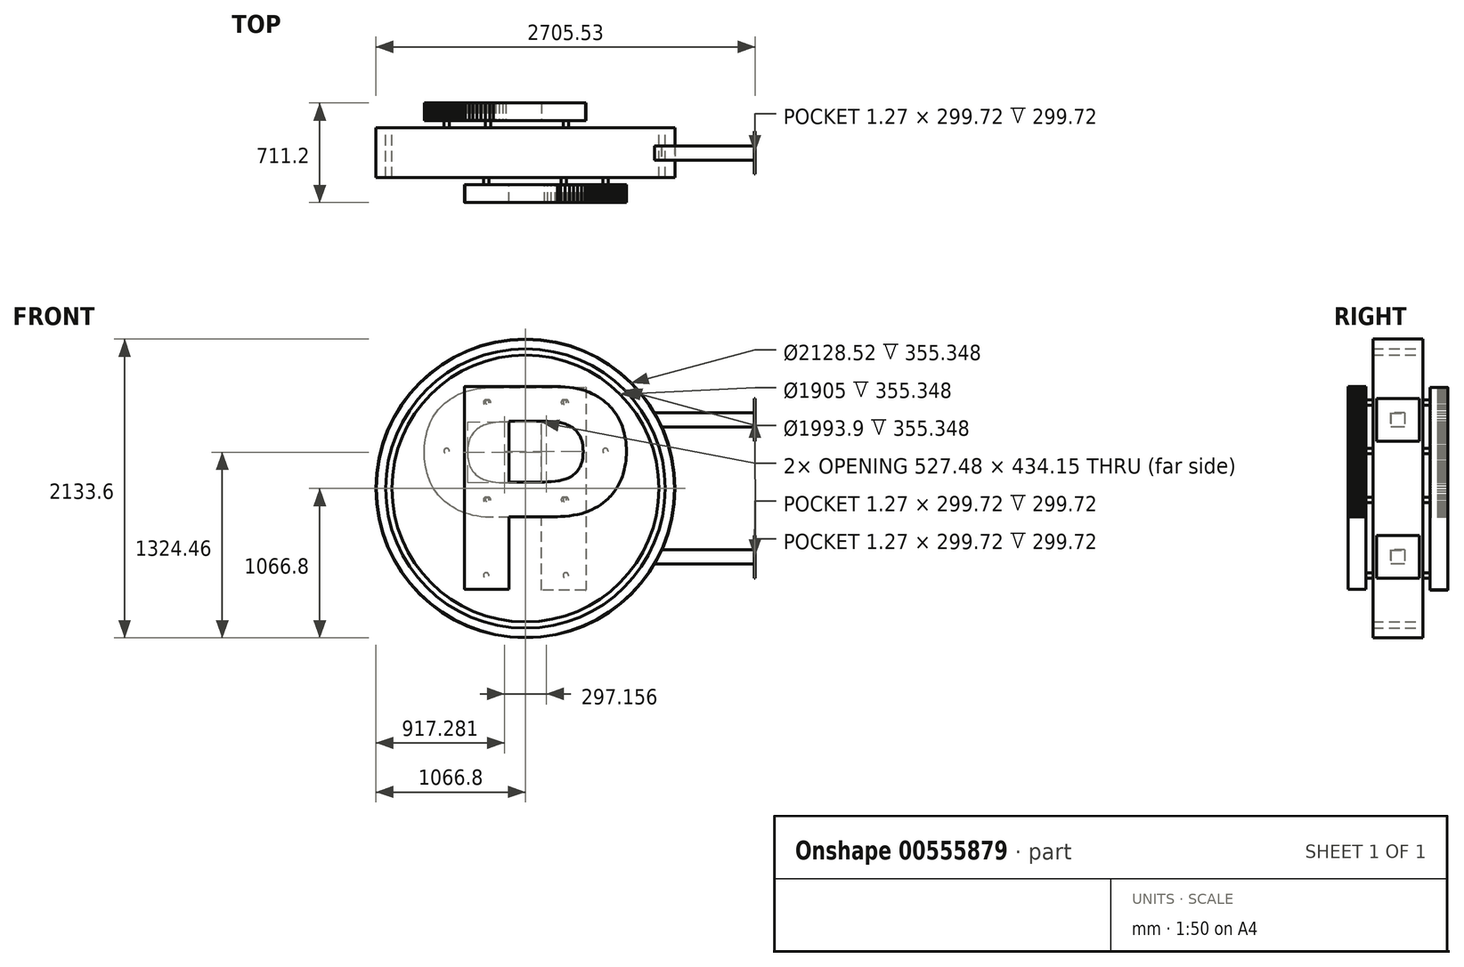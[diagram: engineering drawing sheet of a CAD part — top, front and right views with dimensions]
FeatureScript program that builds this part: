
annotation { "Feature Type Name" : "Feature", "Feature Type Description" : "" }
export const myFeature = defineFeature(function(context is Context, id is Id, definition is map)
    precondition{}
    {
        {
            var Q0;
            Q0=qCreatedBy(makeId("Front.planeOp"),FACE);
            var sketch = newSketch(context, id + "F0", { "sketchPlane" : qUnion([Q0])});
            skCircle(sketch, "E0", {"center": v(-32.18, 27.44) * mm, "radius": 1066.8 * mm});
            skSolve(sketch);
        }
        {
            var Q0;
            Q0 = qSketchRegion(id + "F0", true);
            extrude(context, id + "F1", {"entities" : qUnion([Q0]), "oppositeDirection" : true, "depth" : 355.6 * mm, "offsetDistance" : 25.4 * mm});
        }
        {
            var Q0;
            Q0=qCreatedBy(makeId("Right.planeOp"),FACE);
            var sketch = newSketch(context, id + "F2", { "sketchPlane" : qUnion([Q0])});
            skLineSegment(sketch, "E1.bottom", {"start": v(-1.34, 1094.24) * mm, "end": v(356.95, 1094.24) * mm});
            skLineSegment(sketch, "E1.top", {"start": v(-1.34, -1039.36) * mm, "end": v(356.95, -1039.36) * mm});
            skLineSegment(sketch, "E1.left", {"start": v(-1.34, 1094.24) * mm, "end": v(-1.34, -1039.36) * mm});
            skLineSegment(sketch, "E2", {"start": v(-1.34, 27.44) * mm, "end": v(356.95, 27.44) * mm});
            skLineSegment(sketch, "E3.bottom", {"start": v(125.66, 567.19) * mm, "end": v(227.26, 567.19) * mm});
            skLineSegment(sketch, "E3.top", {"start": v(125.66, 465.59) * mm, "end": v(227.26, 465.59) * mm});
            skLineSegment(sketch, "E3.left", {"start": v(125.66, 567.19) * mm, "end": v(125.66, 465.59) * mm});
            skLineSegment(sketch, "E3.right", {"start": v(227.26, 567.19) * mm, "end": v(227.26, 465.59) * mm});
            skLineSegment(sketch, "E4.bottom", {"start": v(125.66, -410.71) * mm, "end": v(227.26, -410.71) * mm});
            skLineSegment(sketch, "E4.top", {"start": v(125.66, -512.31) * mm, "end": v(227.26, -512.31) * mm});
            skLineSegment(sketch, "E4.left", {"start": v(125.66, -410.71) * mm, "end": v(125.66, -512.31) * mm});
            skLineSegment(sketch, "E4.right", {"start": v(227.26, -410.71) * mm, "end": v(227.26, -512.31) * mm});
            skSolve(sketch);
        }
        {
            var Q0;
            Q0 = qSketchRegion(id + "F2", true);
            extrude(context, id + "F3", {"entities" : qUnion([Q0]), "operationType" : NewBodyOperationType.ADD, "depth" : 1600.2 * mm, "offsetDistance" : 25.4 * mm});
        }
        {
            var Q0;
            Q0=makeQuery(id+"F3.opExtrude","CAP_FACE",FACE,{"disambiguationData":[OSD([sQuery(id+"F2.wireOp",EDGE,"E3.bottom"),sQuery(id+"F2.wireOp",EDGE,"E3.top"),sQuery(id+"F2.wireOp",EDGE,"E3.left"),sQuery(id+"F2.wireOp",EDGE,"E3.right")])],"isStart":false});
            var sketch = newSketch(context, id + "F4", { "sketchPlane" : qUnion([Q0])});
            skLineSegment(sketch, "E5.bottom", {"start": v(25.4, 668.79) * mm, "end": v(330.2, 668.79) * mm});
            skLineSegment(sketch, "E5.top", {"start": v(25.4, 363.99) * mm, "end": v(330.2, 363.99) * mm});
            skLineSegment(sketch, "E5.left", {"start": v(25.4, 668.79) * mm, "end": v(25.4, 363.99) * mm});
            skLineSegment(sketch, "E5.right", {"start": v(330.2, 668.79) * mm, "end": v(330.2, 363.99) * mm});
            skLineSegment(sketch, "E6.bottom", {"start": v(25.4, -309.11) * mm, "end": v(330.2, -309.11) * mm});
            skLineSegment(sketch, "E6.top", {"start": v(25.4, -613.91) * mm, "end": v(330.2, -613.91) * mm});
            skLineSegment(sketch, "E6.left", {"start": v(25.4, -309.11) * mm, "end": v(25.4, -613.91) * mm});
            skLineSegment(sketch, "E6.right", {"start": v(330.2, -309.11) * mm, "end": v(330.2, -613.91) * mm});
            skSolve(sketch);
        }
        {
            var Q0;
            Q0 = qSketchRegion(id + "F4", true);
            extrude(context, id + "F5", {"entities" : qUnion([Q0]), "operationType" : NewBodyOperationType.ADD, "depth" : 6.35 * mm, "offsetDistance" : 25.4 * mm});
        }
        {
            var Q0;
            Q0=makeQuery(id+"F1.opExtrude","CAP_FACE",FACE,{"disambiguationData":[OSD([sQuery(id+"F0.wireOp",EDGE,"E0")])],"isStart":false});
            var sketch = newSketch(context, id + "F6", { "sketchPlane" : qUnion([Q0])});
            skCircle(sketch, "E7", {"center": v(32.18, 27.44) * mm, "radius": 952.5 * mm});
            skCircle(sketch, "E8", {"center": v(32.18, 27.44) * mm, "radius": 996.95 * mm});
            skCircle(sketch, "E9", {"center": v(32.18, 27.44) * mm, "radius": 1066.8 * mm});
            skSolve(sketch);
        }
        {
            var Q0;
            Q0=makeQuery(id+"F1.opExtrude","CAP_FACE",FACE,{"disambiguationData":[OSD([sQuery(id+"F0.wireOp",EDGE,"E0")])],"isStart":false});
            var Q1;
            Q1=makeQuery(id+"F1.opExtrude","CAP_FACE",FACE,{"disambiguationData":[OSD([sQuery(id+"F0.wireOp",EDGE,"E0")])],"isStart":true});
            shell(context, id + "F7", {"entities" : qUnion([Q0, Q1]), "thickness" : 2.54 * mm});
        }
        {
            var Q0;
            Q0=makeQuery(id+"F6.imprint","IMPRINT",FACE,{"disambiguationData":[TD([[makeQuery(id+"F6.imprint","IMPRINT",EDGE,{"derivedFrom":sQuery(id+"F6.wireOp",EDGE,"E8")}),-1.0]])]});
            extrude(context, id + "F8", {"entities" : qUnion([Q0]), "oppositeDirection" : true, "depth" : 355.6 * mm, "offsetDistance" : 25.4 * mm});
        }
        {
            var Q0;
            Q0=makeQuery(id+"F6.imprint","IMPRINT",FACE,{"disambiguationData":[TD([[makeQuery(id+"F6.imprint","IMPRINT",EDGE,{"derivedFrom":sQuery(id+"F6.wireOp",EDGE,"E7")}),-1.0]])]});
            extrude(context, id + "F9", {"entities" : qUnion([Q0]), "oppositeDirection" : true, "depth" : 355.6 * mm, "offsetDistance" : 25.4 * mm});
        }
        {
            var Q0;
            Q0=makeQuery(id+"F6.imprint","IMPRINT",FACE,{"disambiguationData":[TD([[makeQuery(id+"F6.imprint","IMPRINT",EDGE,{"derivedFrom":sQuery(id+"F6.wireOp",EDGE,"E7")}),1.0]])]});
            extrude(context, id + "F10", {"entities" : qUnion([Q0]), "oppositeDirection" : true, "depth" : 355.6 * mm, "offsetDistance" : 25.4 * mm});
        }
        {
            var Q0;
            Q0=makeQuery(id+"F6.imprint","IMPRINT",FACE,{"disambiguationData":[TD([[makeQuery(id+"F6.imprint","IMPRINT",EDGE,{"derivedFrom":sQuery(id+"F6.wireOp",EDGE,"E7")}),1.0]])]});
            var sketch = newSketch(context, id + "F11", { "sketchPlane" : qUnion([Q0])});
            skLineSegment(sketch, "E10", {"start": v(165.47, 68.03) * mm, "end": v(172.25, 68.03) * mm});
            skLineSegment(sketch, "E11", {"start": v(172.25, 68.03) * mm, "end": v(192.6, 68.53) * mm});
            skLineSegment(sketch, "E12", {"start": v(192.6, 68.53) * mm, "end": v(219.22, 70.05) * mm});
            skLineSegment(sketch, "E13", {"start": v(219.22, 70.05) * mm, "end": v(245.35, 72.58) * mm});
            skLineSegment(sketch, "E14", {"start": v(245.35, 72.58) * mm, "end": v(264.58, 75.12) * mm});
            skLineSegment(sketch, "E15", {"start": v(264.58, 75.12) * mm, "end": v(270.97, 76.14) * mm});
            skLineSegment(sketch, "E16", {"start": v(270.97, 76.14) * mm, "end": v(274.1, 76.64) * mm});
            skLineSegment(sketch, "E17", {"start": v(274.1, 76.64) * mm, "end": v(283.45, 78.4) * mm});
            skLineSegment(sketch, "E18", {"start": v(283.45, 78.4) * mm, "end": v(295.55, 81.14) * mm});
            skLineSegment(sketch, "E19", {"start": v(295.55, 81.14) * mm, "end": v(307.28, 84.35) * mm});
            skLineSegment(sketch, "E20", {"start": v(307.28, 84.35) * mm, "end": v(318.63, 88.05) * mm});
            skLineSegment(sketch, "E21", {"start": v(318.63, 88.05) * mm, "end": v(329.6, 92.21) * mm});
            skLineSegment(sketch, "E22", {"start": v(329.6, 92.21) * mm, "end": v(340.19, 96.86) * mm});
            skLineSegment(sketch, "E23", {"start": v(340.19, 96.86) * mm, "end": v(350.4, 101.99) * mm});
            skLineSegment(sketch, "E24", {"start": v(350.4, 101.99) * mm, "end": v(357.81, 106.12) * mm});
            skLineSegment(sketch, "E25", {"start": v(357.81, 106.12) * mm, "end": v(360.23, 107.59) * mm});
            skLineSegment(sketch, "E26", {"start": v(360.23, 107.59) * mm, "end": v(362.62, 109.03) * mm});
            skLineSegment(sketch, "E27", {"start": v(362.62, 109.03) * mm, "end": v(369.62, 113.71) * mm});
            skLineSegment(sketch, "E28", {"start": v(369.62, 113.71) * mm, "end": v(378.54, 120.44) * mm});
            skLineSegment(sketch, "E29", {"start": v(378.54, 120.44) * mm, "end": v(386.99, 127.78) * mm});
            skLineSegment(sketch, "E30", {"start": v(386.99, 127.78) * mm, "end": v(394.96, 135.73) * mm});
            skLineSegment(sketch, "E31", {"start": v(394.96, 135.73) * mm, "end": v(402.46, 144.27) * mm});
            skLineSegment(sketch, "E32", {"start": v(402.46, 144.27) * mm, "end": v(409.49, 153.42) * mm});
            skLineSegment(sketch, "E33", {"start": v(409.49, 153.42) * mm, "end": v(416.04, 163.17) * mm});
            skLineSegment(sketch, "E34", {"start": v(416.04, 163.17) * mm, "end": v(420.67, 170.88) * mm});
            skLineSegment(sketch, "E35", {"start": v(420.67, 170.88) * mm, "end": v(422.11, 173.52) * mm});
            skLineSegment(sketch, "E36", {"start": v(422.11, 173.52) * mm, "end": v(423.59, 176.22) * mm});
            skLineSegment(sketch, "E37", {"start": v(423.59, 176.22) * mm, "end": v(427.57, 184.58) * mm});
            skLineSegment(sketch, "E38", {"start": v(427.57, 184.58) * mm, "end": v(432.3, 196.47) * mm});
            skLineSegment(sketch, "E39", {"start": v(432.3, 196.47) * mm, "end": v(436.32, 209.18) * mm});
            skLineSegment(sketch, "E40", {"start": v(436.32, 209.18) * mm, "end": v(439.6, 222.71) * mm});
            skLineSegment(sketch, "E41", {"start": v(439.6, 222.71) * mm, "end": v(442.15, 237.07) * mm});
            skLineSegment(sketch, "E42", {"start": v(442.15, 237.07) * mm, "end": v(443.98, 252.26) * mm});
            skLineSegment(sketch, "E43", {"start": v(443.98, 252.26) * mm, "end": v(445.07, 268.26) * mm});
            skLineSegment(sketch, "E44", {"start": v(445.07, 268.26) * mm, "end": v(445.44, 280.9) * mm});
            skLineSegment(sketch, "E45", {"start": v(445.44, 280.9) * mm, "end": v(445.44, 285.1) * mm});
            skLineSegment(sketch, "E46", {"start": v(445.44, 285.1) * mm, "end": v(445.44, 289.3) * mm});
            skLineSegment(sketch, "E47", {"start": v(445.44, 289.3) * mm, "end": v(445.07, 301.93) * mm});
            skLineSegment(sketch, "E48", {"start": v(445.07, 301.93) * mm, "end": v(443.98, 317.93) * mm});
            skLineSegment(sketch, "E49", {"start": v(443.98, 317.93) * mm, "end": v(442.15, 333.12) * mm});
            skLineSegment(sketch, "E50", {"start": v(442.15, 333.12) * mm, "end": v(439.6, 347.48) * mm});
            skLineSegment(sketch, "E51", {"start": v(439.6, 347.48) * mm, "end": v(436.32, 361.02) * mm});
            skLineSegment(sketch, "E52", {"start": v(436.32, 361.02) * mm, "end": v(432.3, 373.73) * mm});
            skLineSegment(sketch, "E53", {"start": v(432.3, 373.73) * mm, "end": v(427.57, 385.62) * mm});
            skLineSegment(sketch, "E54", {"start": v(427.57, 385.62) * mm, "end": v(423.59, 393.98) * mm});
            skLineSegment(sketch, "E55", {"start": v(423.59, 393.98) * mm, "end": v(422.11, 396.68) * mm});
            skLineSegment(sketch, "E56", {"start": v(422.11, 396.68) * mm, "end": v(420.67, 399.32) * mm});
            skLineSegment(sketch, "E57", {"start": v(420.67, 399.32) * mm, "end": v(416.04, 407.03) * mm});
            skLineSegment(sketch, "E58", {"start": v(416.04, 407.03) * mm, "end": v(409.49, 416.78) * mm});
            skLineSegment(sketch, "E59", {"start": v(409.49, 416.78) * mm, "end": v(402.46, 425.92) * mm});
            skLineSegment(sketch, "E60", {"start": v(402.46, 425.92) * mm, "end": v(394.96, 434.47) * mm});
            skLineSegment(sketch, "E61", {"start": v(394.96, 434.47) * mm, "end": v(386.99, 442.4) * mm});
            skLineSegment(sketch, "E62", {"start": v(386.99, 442.4) * mm, "end": v(378.54, 449.74) * mm});
            skLineSegment(sketch, "E63", {"start": v(378.54, 449.74) * mm, "end": v(369.62, 456.49) * mm});
            skLineSegment(sketch, "E64", {"start": v(369.62, 456.49) * mm, "end": v(362.62, 461.17) * mm});
            skLineSegment(sketch, "E65", {"start": v(362.62, 461.17) * mm, "end": v(360.23, 462.62) * mm});
            skLineSegment(sketch, "E66", {"start": v(360.23, 462.62) * mm, "end": v(357.81, 464.09) * mm});
            skLineSegment(sketch, "E67", {"start": v(357.81, 464.09) * mm, "end": v(350.4, 468.2) * mm});
            skLineSegment(sketch, "E68", {"start": v(350.4, 468.2) * mm, "end": v(340.19, 473.32) * mm});
            skLineSegment(sketch, "E69", {"start": v(340.19, 473.32) * mm, "end": v(329.6, 477.97) * mm});
            skLineSegment(sketch, "E70", {"start": v(329.6, 477.97) * mm, "end": v(318.63, 482.13) * mm});
            skLineSegment(sketch, "E71", {"start": v(318.63, 482.13) * mm, "end": v(307.28, 485.83) * mm});
            skLineSegment(sketch, "E72", {"start": v(307.28, 485.83) * mm, "end": v(295.55, 489.05) * mm});
            skLineSegment(sketch, "E73", {"start": v(295.55, 489.05) * mm, "end": v(283.45, 491.8) * mm});
            skLineSegment(sketch, "E74", {"start": v(283.45, 491.8) * mm, "end": v(274.1, 493.56) * mm});
            skLineSegment(sketch, "E75", {"start": v(274.1, 493.56) * mm, "end": v(270.97, 494.06) * mm});
            skLineSegment(sketch, "E76", {"start": v(270.97, 494.06) * mm, "end": v(264.58, 495.08) * mm});
            skLineSegment(sketch, "E77", {"start": v(264.58, 495.08) * mm, "end": v(245.35, 497.6) * mm});
            skLineSegment(sketch, "E78", {"start": v(245.35, 497.6) * mm, "end": v(219.22, 500.15) * mm});
            skLineSegment(sketch, "E79", {"start": v(219.22, 500.15) * mm, "end": v(192.6, 501.67) * mm});
            skLineSegment(sketch, "E80", {"start": v(192.6, 501.67) * mm, "end": v(172.25, 502.18) * mm});
            skLineSegment(sketch, "E81", {"start": v(172.25, 502.18) * mm, "end": v(165.47, 502.18) * mm});
            skLineSegment(sketch, "E82", {"start": v(165.47, 502.18) * mm, "end": v(-82.04, 502.18) * mm});
            skLineSegment(sketch, "E83", {"start": v(-82.04, 502.18) * mm, "end": v(-82.04, 68.03) * mm});
            skLineSegment(sketch, "E84", {"start": v(-82.04, 68.03) * mm, "end": v(165.47, 68.03) * mm});
            skLineSegment(sketch, "E85", {"start": v(252.7, 749.7) * mm, "end": v(261.04, 749.7) * mm});
            skLineSegment(sketch, "E86", {"start": v(261.04, 749.7) * mm, "end": v(286.04, 749.08) * mm});
            skLineSegment(sketch, "E87", {"start": v(286.04, 749.08) * mm, "end": v(318.12, 747.22) * mm});
            skLineSegment(sketch, "E88", {"start": v(318.12, 747.22) * mm, "end": v(348.93, 744.13) * mm});
            skLineSegment(sketch, "E89", {"start": v(348.93, 744.13) * mm, "end": v(378.48, 739.8) * mm});
            skLineSegment(sketch, "E90", {"start": v(378.48, 739.8) * mm, "end": v(406.75, 734.24) * mm});
            skLineSegment(sketch, "E91", {"start": v(406.75, 734.24) * mm, "end": v(433.76, 727.44) * mm});
            skLineSegment(sketch, "E92", {"start": v(433.76, 727.44) * mm, "end": v(459.5, 719.4) * mm});
            skLineSegment(sketch, "E93", {"start": v(459.5, 719.4) * mm, "end": v(477.94, 712.64) * mm});
            skLineSegment(sketch, "E94", {"start": v(477.94, 712.64) * mm, "end": v(483.99, 710.13) * mm});
            skLineSegment(sketch, "E95", {"start": v(483.99, 710.13) * mm, "end": v(489.86, 707.7) * mm});
            skLineSegment(sketch, "E96", {"start": v(489.86, 707.7) * mm, "end": v(507.26, 699.85) * mm});
            skLineSegment(sketch, "E97", {"start": v(507.26, 699.85) * mm, "end": v(529.44, 688.76) * mm});
            skLineSegment(sketch, "E98", {"start": v(529.44, 688.76) * mm, "end": v(550.5, 676.9) * mm});
            skLineSegment(sketch, "E99", {"start": v(550.5, 676.9) * mm, "end": v(570.46, 664.23) * mm});
            skLineSegment(sketch, "E100", {"start": v(570.46, 664.23) * mm, "end": v(589.3, 650.77) * mm});
            skLineSegment(sketch, "E101", {"start": v(589.3, 650.77) * mm, "end": v(607.04, 636.52) * mm});
            skLineSegment(sketch, "E102", {"start": v(607.04, 636.52) * mm, "end": v(623.67, 621.48) * mm});
            skLineSegment(sketch, "E103", {"start": v(623.67, 621.48) * mm, "end": v(635.43, 609.72) * mm});
            skLineSegment(sketch, "E104", {"start": v(635.43, 609.72) * mm, "end": v(639.2, 605.65) * mm});
            skLineSegment(sketch, "E105", {"start": v(639.2, 605.65) * mm, "end": v(642.9, 601.62) * mm});
            skLineSegment(sketch, "E106", {"start": v(642.9, 601.62) * mm, "end": v(653.63, 589.13) * mm});
            skLineSegment(sketch, "E107", {"start": v(653.63, 589.13) * mm, "end": v(667.07, 572.04) * mm});
            skLineSegment(sketch, "E108", {"start": v(667.07, 572.04) * mm, "end": v(679.5, 554.38) * mm});
            skLineSegment(sketch, "E109", {"start": v(679.5, 554.38) * mm, "end": v(690.91, 536.15) * mm});
            skLineSegment(sketch, "E110", {"start": v(690.91, 536.15) * mm, "end": v(701.31, 517.35) * mm});
            skLineSegment(sketch, "E111", {"start": v(701.31, 517.35) * mm, "end": v(710.7, 497.99) * mm});
            skLineSegment(sketch, "E112", {"start": v(710.7, 497.99) * mm, "end": v(719.07, 478.05) * mm});
            skLineSegment(sketch, "E113", {"start": v(719.07, 478.05) * mm, "end": v(724.72, 462.72) * mm});
            skLineSegment(sketch, "E114", {"start": v(724.72, 462.72) * mm, "end": v(726.42, 457.55) * mm});
            skLineSegment(sketch, "E115", {"start": v(726.42, 457.55) * mm, "end": v(728.13, 452.36) * mm});
            skLineSegment(sketch, "E116", {"start": v(728.13, 452.36) * mm, "end": v(732.84, 436.65) * mm});
            skLineSegment(sketch, "E117", {"start": v(732.84, 436.65) * mm, "end": v(738.4, 415.56) * mm});
            skLineSegment(sketch, "E118", {"start": v(738.4, 415.56) * mm, "end": v(743.11, 394.3) * mm});
            skLineSegment(sketch, "E119", {"start": v(743.11, 394.3) * mm, "end": v(746.97, 372.83) * mm});
            skLineSegment(sketch, "E120", {"start": v(746.97, 372.83) * mm, "end": v(749.96, 351.19) * mm});
            skLineSegment(sketch, "E121", {"start": v(749.96, 351.19) * mm, "end": v(752.1, 329.35) * mm});
            skLineSegment(sketch, "E122", {"start": v(752.1, 329.35) * mm, "end": v(753.38, 307.32) * mm});
            skLineSegment(sketch, "E123", {"start": v(753.38, 307.32) * mm, "end": v(753.81, 290.65) * mm});
            skLineSegment(sketch, "E124", {"start": v(753.81, 290.65) * mm, "end": v(753.81, 285.1) * mm});
            skLineSegment(sketch, "E125", {"start": v(753.81, 285.1) * mm, "end": v(753.81, 279.66) * mm});
            skLineSegment(sketch, "E126", {"start": v(753.81, 279.66) * mm, "end": v(753.38, 263.33) * mm});
            skLineSegment(sketch, "E127", {"start": v(753.38, 263.33) * mm, "end": v(752.1, 241.67) * mm});
            skLineSegment(sketch, "E128", {"start": v(752.1, 241.67) * mm, "end": v(749.96, 220.1) * mm});
            skLineSegment(sketch, "E129", {"start": v(749.96, 220.1) * mm, "end": v(746.97, 198.61) * mm});
            skLineSegment(sketch, "E130", {"start": v(746.97, 198.61) * mm, "end": v(743.11, 177.23) * mm});
            skLineSegment(sketch, "E131", {"start": v(743.11, 177.23) * mm, "end": v(738.4, 155.95) * mm});
            skLineSegment(sketch, "E132", {"start": v(738.4, 155.95) * mm, "end": v(732.84, 134.76) * mm});
            skLineSegment(sketch, "E133", {"start": v(732.84, 134.76) * mm, "end": v(728.13, 118.9) * mm});
            skLineSegment(sketch, "E134", {"start": v(728.13, 118.9) * mm, "end": v(726.42, 113.67) * mm});
            skLineSegment(sketch, "E135", {"start": v(726.42, 113.67) * mm, "end": v(724.72, 108.44) * mm});
            skLineSegment(sketch, "E136", {"start": v(724.72, 108.44) * mm, "end": v(719.07, 92.92) * mm});
            skLineSegment(sketch, "E137", {"start": v(719.07, 92.92) * mm, "end": v(710.7, 72.77) * mm});
            skLineSegment(sketch, "E138", {"start": v(710.7, 72.77) * mm, "end": v(701.31, 53.23) * mm});
            skLineSegment(sketch, "E139", {"start": v(701.31, 53.23) * mm, "end": v(690.91, 34.28) * mm});
            skLineSegment(sketch, "E140", {"start": v(690.91, 34.28) * mm, "end": v(679.5, 15.95) * mm});
            skLineSegment(sketch, "E141", {"start": v(679.5, 15.95) * mm, "end": v(667.07, -1.79) * mm});
            skLineSegment(sketch, "E142", {"start": v(667.07, -1.79) * mm, "end": v(653.63, -18.92) * mm});
            skLineSegment(sketch, "E143", {"start": v(653.63, -18.92) * mm, "end": v(642.9, -31.41) * mm});
            skLineSegment(sketch, "E144", {"start": v(642.9, -31.41) * mm, "end": v(639.2, -35.44) * mm});
            skLineSegment(sketch, "E145", {"start": v(639.2, -35.44) * mm, "end": v(635.43, -39.52) * mm});
            skLineSegment(sketch, "E146", {"start": v(635.43, -39.52) * mm, "end": v(623.67, -51.29) * mm});
            skLineSegment(sketch, "E147", {"start": v(623.67, -51.29) * mm, "end": v(607.04, -66.33) * mm});
            skLineSegment(sketch, "E148", {"start": v(607.04, -66.33) * mm, "end": v(589.3, -80.58) * mm});
            skLineSegment(sketch, "E149", {"start": v(589.3, -80.58) * mm, "end": v(570.46, -94.03) * mm});
            skLineSegment(sketch, "E150", {"start": v(570.46, -94.03) * mm, "end": v(550.5, -106.7) * mm});
            skLineSegment(sketch, "E151", {"start": v(550.5, -106.7) * mm, "end": v(529.44, -118.56) * mm});
            skLineSegment(sketch, "E152", {"start": v(529.44, -118.56) * mm, "end": v(507.26, -129.64) * mm});
            skLineSegment(sketch, "E153", {"start": v(507.26, -129.64) * mm, "end": v(489.86, -137.5) * mm});
            skLineSegment(sketch, "E154", {"start": v(489.86, -137.5) * mm, "end": v(483.99, -139.93) * mm});
            skLineSegment(sketch, "E155", {"start": v(483.99, -139.93) * mm, "end": v(477.94, -142.44) * mm});
            skLineSegment(sketch, "E156", {"start": v(477.94, -142.44) * mm, "end": v(459.5, -149.2) * mm});
            skLineSegment(sketch, "E157", {"start": v(459.5, -149.2) * mm, "end": v(433.76, -157.24) * mm});
            skLineSegment(sketch, "E158", {"start": v(433.76, -157.24) * mm, "end": v(406.75, -164.04) * mm});
            skLineSegment(sketch, "E159", {"start": v(406.75, -164.04) * mm, "end": v(378.48, -169.6) * mm});
            skLineSegment(sketch, "E160", {"start": v(378.48, -169.6) * mm, "end": v(348.93, -173.93) * mm});
            skLineSegment(sketch, "E161", {"start": v(348.93, -173.93) * mm, "end": v(318.12, -177.02) * mm});
            skLineSegment(sketch, "E162", {"start": v(318.12, -177.02) * mm, "end": v(286.04, -178.87) * mm});
            skLineSegment(sketch, "E163", {"start": v(286.04, -178.87) * mm, "end": v(261.04, -179.5) * mm});
            skLineSegment(sketch, "E164", {"start": v(261.04, -179.5) * mm, "end": v(252.7, -179.5) * mm});
            skLineSegment(sketch, "E165", {"start": v(252.7, -179.5) * mm, "end": v(-82.04, -179.5) * mm});
            skLineSegment(sketch, "E166", {"start": v(-82.04, -179.5) * mm, "end": v(-82.04, -698.86) * mm});
            skLineSegment(sketch, "E167", {"start": v(-82.04, -698.86) * mm, "end": v(-400.56, -698.86) * mm});
            skLineSegment(sketch, "E168", {"start": v(-400.56, -698.86) * mm, "end": v(-400.56, 749.7) * mm});
            skLineSegment(sketch, "E169", {"start": v(-400.56, 749.7) * mm, "end": v(252.7, 749.7) * mm});
            skCircle(sketch, "E170", {"center": v(32.68, 25.72) * mm, "radius": 842.23 * mm});
            skSolve(sketch);
        }
        {
            var Q0;
            Q0=makeQuery(id+"F11.imprint","IMPRINT",FACE,{"disambiguationData":[TD([[makeQuery(id+"F11.imprint","IMPRINT",EDGE,{"derivedFrom":sQuery(id+"F11.wireOp",EDGE,"E10")}),-1.0]])]});
            extrude(context, id + "F12", {"entities" : qUnion([Q0]), "depth" : 177.8 * mm, "offsetDistance" : 25.4 * mm});
        }
        {
            var Q0;
            Q0=makeQuery(id+"F10.opExtrude","CAP_FACE",FACE,{"disambiguationData":[OSD([sQuery(id+"F6.wireOp",EDGE,"E7")])],"isStart":false});
            var sketch = newSketch(context, id + "F13", { "sketchPlane" : qUnion([Q0])});
            skLineSegment(sketch, "E171", {"start": v(99.23, 73.84) * mm, "end": v(106, 73.84) * mm});
            skLineSegment(sketch, "E172", {"start": v(106, 73.84) * mm, "end": v(126.36, 74.35) * mm});
            skLineSegment(sketch, "E173", {"start": v(126.36, 74.35) * mm, "end": v(152.98, 75.87) * mm});
            skLineSegment(sketch, "E174", {"start": v(152.98, 75.87) * mm, "end": v(179.1, 78.4) * mm});
            skLineSegment(sketch, "E175", {"start": v(179.1, 78.4) * mm, "end": v(198.34, 80.93) * mm});
            skLineSegment(sketch, "E176", {"start": v(198.34, 80.93) * mm, "end": v(204.72, 81.96) * mm});
            skLineSegment(sketch, "E177", {"start": v(204.72, 81.96) * mm, "end": v(207.85, 82.45) * mm});
            skLineSegment(sketch, "E178", {"start": v(207.85, 82.45) * mm, "end": v(217.2, 84.21) * mm});
            skLineSegment(sketch, "E179", {"start": v(217.2, 84.21) * mm, "end": v(229.3, 86.95) * mm});
            skLineSegment(sketch, "E180", {"start": v(229.3, 86.95) * mm, "end": v(241.04, 90.17) * mm});
            skLineSegment(sketch, "E181", {"start": v(241.04, 90.17) * mm, "end": v(252.38, 93.86) * mm});
            skLineSegment(sketch, "E182", {"start": v(252.38, 93.86) * mm, "end": v(263.36, 98.03) * mm});
            skLineSegment(sketch, "E183", {"start": v(263.36, 98.03) * mm, "end": v(273.94, 102.68) * mm});
            skLineSegment(sketch, "E184", {"start": v(273.94, 102.68) * mm, "end": v(284.16, 107.8) * mm});
            skLineSegment(sketch, "E185", {"start": v(284.16, 107.8) * mm, "end": v(291.57, 111.94) * mm});
            skLineSegment(sketch, "E186", {"start": v(291.57, 111.94) * mm, "end": v(293.99, 113.4) * mm});
            skLineSegment(sketch, "E187", {"start": v(293.99, 113.4) * mm, "end": v(296.38, 114.85) * mm});
            skLineSegment(sketch, "E188", {"start": v(296.38, 114.85) * mm, "end": v(303.38, 119.53) * mm});
            skLineSegment(sketch, "E189", {"start": v(303.38, 119.53) * mm, "end": v(312.3, 126.26) * mm});
            skLineSegment(sketch, "E190", {"start": v(312.3, 126.26) * mm, "end": v(320.75, 133.6) * mm});
            skLineSegment(sketch, "E191", {"start": v(320.75, 133.6) * mm, "end": v(328.72, 141.54) * mm});
            skLineSegment(sketch, "E192", {"start": v(328.72, 141.54) * mm, "end": v(336.22, 150.09) * mm});
            skLineSegment(sketch, "E193", {"start": v(336.22, 150.09) * mm, "end": v(343.24, 159.24) * mm});
            skLineSegment(sketch, "E194", {"start": v(343.24, 159.24) * mm, "end": v(349.8, 168.98) * mm});
            skLineSegment(sketch, "E195", {"start": v(349.8, 168.98) * mm, "end": v(354.43, 176.7) * mm});
            skLineSegment(sketch, "E196", {"start": v(354.43, 176.7) * mm, "end": v(355.87, 179.33) * mm});
            skLineSegment(sketch, "E197", {"start": v(355.87, 179.33) * mm, "end": v(357.35, 182.04) * mm});
            skLineSegment(sketch, "E198", {"start": v(357.35, 182.04) * mm, "end": v(361.33, 190.4) * mm});
            skLineSegment(sketch, "E199", {"start": v(361.33, 190.4) * mm, "end": v(366.07, 202.29) * mm});
            skLineSegment(sketch, "E200", {"start": v(366.07, 202.29) * mm, "end": v(370.08, 215) * mm});
            skLineSegment(sketch, "E201", {"start": v(370.08, 215) * mm, "end": v(373.36, 228.53) * mm});
            skLineSegment(sketch, "E202", {"start": v(373.36, 228.53) * mm, "end": v(375.91, 242.9) * mm});
            skLineSegment(sketch, "E203", {"start": v(375.91, 242.9) * mm, "end": v(377.73, 258.07) * mm});
            skLineSegment(sketch, "E204", {"start": v(377.73, 258.07) * mm, "end": v(378.83, 274.08) * mm});
            skLineSegment(sketch, "E205", {"start": v(378.83, 274.08) * mm, "end": v(379.2, 286.7) * mm});
            skLineSegment(sketch, "E206", {"start": v(379.2, 286.7) * mm, "end": v(379.2, 290.92) * mm});
            skLineSegment(sketch, "E207", {"start": v(379.2, 290.92) * mm, "end": v(379.2, 295.12) * mm});
            skLineSegment(sketch, "E208", {"start": v(379.2, 295.12) * mm, "end": v(378.83, 307.74) * mm});
            skLineSegment(sketch, "E209", {"start": v(378.83, 307.74) * mm, "end": v(377.73, 323.75) * mm});
            skLineSegment(sketch, "E210", {"start": v(377.73, 323.75) * mm, "end": v(375.91, 338.93) * mm});
            skLineSegment(sketch, "E211", {"start": v(375.91, 338.93) * mm, "end": v(373.36, 353.3) * mm});
            skLineSegment(sketch, "E212", {"start": v(373.36, 353.3) * mm, "end": v(370.08, 366.83) * mm});
            skLineSegment(sketch, "E213", {"start": v(370.08, 366.83) * mm, "end": v(366.07, 379.55) * mm});
            skLineSegment(sketch, "E214", {"start": v(366.07, 379.55) * mm, "end": v(361.33, 391.44) * mm});
            skLineSegment(sketch, "E215", {"start": v(361.33, 391.44) * mm, "end": v(357.35, 399.8) * mm});
            skLineSegment(sketch, "E216", {"start": v(357.35, 399.8) * mm, "end": v(355.87, 402.5) * mm});
            skLineSegment(sketch, "E217", {"start": v(355.87, 402.5) * mm, "end": v(354.43, 405.13) * mm});
            skLineSegment(sketch, "E218", {"start": v(354.43, 405.13) * mm, "end": v(349.8, 412.85) * mm});
            skLineSegment(sketch, "E219", {"start": v(349.8, 412.85) * mm, "end": v(343.24, 422.6) * mm});
            skLineSegment(sketch, "E220", {"start": v(343.24, 422.6) * mm, "end": v(336.22, 431.74) * mm});
            skLineSegment(sketch, "E221", {"start": v(336.22, 431.74) * mm, "end": v(328.72, 440.29) * mm});
            skLineSegment(sketch, "E222", {"start": v(328.72, 440.29) * mm, "end": v(320.75, 448.22) * mm});
            skLineSegment(sketch, "E223", {"start": v(320.75, 448.22) * mm, "end": v(312.3, 455.56) * mm});
            skLineSegment(sketch, "E224", {"start": v(312.3, 455.56) * mm, "end": v(303.38, 462.3) * mm});
            skLineSegment(sketch, "E225", {"start": v(303.38, 462.3) * mm, "end": v(296.38, 466.99) * mm});
            skLineSegment(sketch, "E226", {"start": v(296.38, 466.99) * mm, "end": v(293.99, 468.44) * mm});
            skLineSegment(sketch, "E227", {"start": v(293.99, 468.44) * mm, "end": v(291.57, 469.9) * mm});
            skLineSegment(sketch, "E228", {"start": v(291.57, 469.9) * mm, "end": v(284.16, 474.03) * mm});
            skLineSegment(sketch, "E229", {"start": v(284.16, 474.03) * mm, "end": v(273.94, 479.14) * mm});
            skLineSegment(sketch, "E230", {"start": v(273.94, 479.14) * mm, "end": v(263.36, 483.78) * mm});
            skLineSegment(sketch, "E231", {"start": v(263.36, 483.78) * mm, "end": v(252.38, 487.95) * mm});
            skLineSegment(sketch, "E232", {"start": v(252.38, 487.95) * mm, "end": v(241.04, 491.65) * mm});
            skLineSegment(sketch, "E233", {"start": v(241.04, 491.65) * mm, "end": v(229.3, 494.87) * mm});
            skLineSegment(sketch, "E234", {"start": v(229.3, 494.87) * mm, "end": v(217.2, 497.6) * mm});
            skLineSegment(sketch, "E235", {"start": v(217.2, 497.6) * mm, "end": v(207.85, 499.38) * mm});
            skLineSegment(sketch, "E236", {"start": v(207.85, 499.38) * mm, "end": v(204.72, 499.88) * mm});
            skLineSegment(sketch, "E237", {"start": v(204.72, 499.88) * mm, "end": v(198.34, 500.9) * mm});
            skLineSegment(sketch, "E238", {"start": v(198.34, 500.9) * mm, "end": v(179.1, 503.42) * mm});
            skLineSegment(sketch, "E239", {"start": v(179.1, 503.42) * mm, "end": v(152.98, 505.96) * mm});
            skLineSegment(sketch, "E240", {"start": v(152.98, 505.96) * mm, "end": v(126.36, 507.5) * mm});
            skLineSegment(sketch, "E241", {"start": v(126.36, 507.5) * mm, "end": v(106, 508) * mm});
            skLineSegment(sketch, "E242", {"start": v(106, 508) * mm, "end": v(99.23, 508) * mm});
            skLineSegment(sketch, "E243", {"start": v(99.23, 508) * mm, "end": v(-148.28, 508) * mm});
            skLineSegment(sketch, "E244", {"start": v(-148.28, 508) * mm, "end": v(-148.28, 73.84) * mm});
            skLineSegment(sketch, "E245", {"start": v(-148.28, 73.84) * mm, "end": v(99.23, 73.84) * mm});
            skLineSegment(sketch, "E246", {"start": v(186.46, 755.51) * mm, "end": v(194.8, 755.51) * mm});
            skLineSegment(sketch, "E247", {"start": v(194.8, 755.51) * mm, "end": v(219.8, 754.9) * mm});
            skLineSegment(sketch, "E248", {"start": v(219.8, 754.9) * mm, "end": v(251.88, 753.04) * mm});
            skLineSegment(sketch, "E249", {"start": v(251.88, 753.04) * mm, "end": v(282.69, 749.95) * mm});
            skLineSegment(sketch, "E250", {"start": v(282.69, 749.95) * mm, "end": v(312.23, 745.62) * mm});
            skLineSegment(sketch, "E251", {"start": v(312.23, 745.62) * mm, "end": v(340.51, 740.06) * mm});
            skLineSegment(sketch, "E252", {"start": v(340.51, 740.06) * mm, "end": v(367.52, 733.26) * mm});
            skLineSegment(sketch, "E253", {"start": v(367.52, 733.26) * mm, "end": v(393.26, 725.22) * mm});
            skLineSegment(sketch, "E254", {"start": v(393.26, 725.22) * mm, "end": v(411.7, 718.46) * mm});
            skLineSegment(sketch, "E255", {"start": v(411.7, 718.46) * mm, "end": v(417.74, 715.95) * mm});
            skLineSegment(sketch, "E256", {"start": v(417.74, 715.95) * mm, "end": v(423.62, 713.51) * mm});
            skLineSegment(sketch, "E257", {"start": v(423.62, 713.51) * mm, "end": v(441.02, 705.66) * mm});
            skLineSegment(sketch, "E258", {"start": v(441.02, 705.66) * mm, "end": v(463.2, 694.58) * mm});
            skLineSegment(sketch, "E259", {"start": v(463.2, 694.58) * mm, "end": v(484.26, 682.7) * mm});
            skLineSegment(sketch, "E260", {"start": v(484.26, 682.7) * mm, "end": v(504.21, 670.05) * mm});
            skLineSegment(sketch, "E261", {"start": v(504.21, 670.05) * mm, "end": v(523.06, 656.59) * mm});
            skLineSegment(sketch, "E262", {"start": v(523.06, 656.59) * mm, "end": v(540.8, 642.34) * mm});
            skLineSegment(sketch, "E263", {"start": v(540.8, 642.34) * mm, "end": v(557.43, 627.3) * mm});
            skLineSegment(sketch, "E264", {"start": v(557.43, 627.3) * mm, "end": v(569.2, 615.54) * mm});
            skLineSegment(sketch, "E265", {"start": v(569.2, 615.54) * mm, "end": v(572.95, 611.47) * mm});
            skLineSegment(sketch, "E266", {"start": v(572.95, 611.47) * mm, "end": v(576.66, 607.43) * mm});
            skLineSegment(sketch, "E267", {"start": v(576.66, 607.43) * mm, "end": v(587.4, 594.94) * mm});
            skLineSegment(sketch, "E268", {"start": v(587.4, 594.94) * mm, "end": v(600.83, 577.85) * mm});
            skLineSegment(sketch, "E269", {"start": v(600.83, 577.85) * mm, "end": v(613.26, 560.2) * mm});
            skLineSegment(sketch, "E270", {"start": v(613.26, 560.2) * mm, "end": v(624.67, 541.97) * mm});
            skLineSegment(sketch, "E271", {"start": v(624.67, 541.97) * mm, "end": v(635.07, 523.17) * mm});
            skLineSegment(sketch, "E272", {"start": v(635.07, 523.17) * mm, "end": v(644.45, 503.8) * mm});
            skLineSegment(sketch, "E273", {"start": v(644.45, 503.8) * mm, "end": v(652.83, 483.87) * mm});
            skLineSegment(sketch, "E274", {"start": v(652.83, 483.87) * mm, "end": v(658.48, 468.53) * mm});
            skLineSegment(sketch, "E275", {"start": v(658.48, 468.53) * mm, "end": v(660.18, 463.36) * mm});
            skLineSegment(sketch, "E276", {"start": v(660.18, 463.36) * mm, "end": v(661.89, 458.17) * mm});
            skLineSegment(sketch, "E277", {"start": v(661.89, 458.17) * mm, "end": v(666.6, 442.47) * mm});
            skLineSegment(sketch, "E278", {"start": v(666.6, 442.47) * mm, "end": v(672.17, 421.38) * mm});
            skLineSegment(sketch, "E279", {"start": v(672.17, 421.38) * mm, "end": v(676.87, 400.11) * mm});
            skLineSegment(sketch, "E280", {"start": v(676.87, 400.11) * mm, "end": v(680.73, 378.65) * mm});
            skLineSegment(sketch, "E281", {"start": v(680.73, 378.65) * mm, "end": v(683.72, 357) * mm});
            skLineSegment(sketch, "E282", {"start": v(683.72, 357) * mm, "end": v(685.86, 335.16) * mm});
            skLineSegment(sketch, "E283", {"start": v(685.86, 335.16) * mm, "end": v(687.14, 313.13) * mm});
            skLineSegment(sketch, "E284", {"start": v(687.14, 313.13) * mm, "end": v(687.57, 296.47) * mm});
            skLineSegment(sketch, "E285", {"start": v(687.57, 296.47) * mm, "end": v(687.57, 290.92) * mm});
            skLineSegment(sketch, "E286", {"start": v(687.57, 290.92) * mm, "end": v(687.57, 285.48) * mm});
            skLineSegment(sketch, "E287", {"start": v(687.57, 285.48) * mm, "end": v(687.14, 269.15) * mm});
            skLineSegment(sketch, "E288", {"start": v(687.14, 269.15) * mm, "end": v(685.86, 247.48) * mm});
            skLineSegment(sketch, "E289", {"start": v(685.86, 247.48) * mm, "end": v(683.72, 225.91) * mm});
            skLineSegment(sketch, "E290", {"start": v(683.72, 225.91) * mm, "end": v(680.73, 204.43) * mm});
            skLineSegment(sketch, "E291", {"start": v(680.73, 204.43) * mm, "end": v(676.87, 183.05) * mm});
            skLineSegment(sketch, "E292", {"start": v(676.87, 183.05) * mm, "end": v(672.17, 161.77) * mm});
            skLineSegment(sketch, "E293", {"start": v(672.17, 161.77) * mm, "end": v(666.6, 140.58) * mm});
            skLineSegment(sketch, "E294", {"start": v(666.6, 140.58) * mm, "end": v(661.89, 124.73) * mm});
            skLineSegment(sketch, "E295", {"start": v(661.89, 124.73) * mm, "end": v(660.18, 119.49) * mm});
            skLineSegment(sketch, "E296", {"start": v(660.18, 119.49) * mm, "end": v(658.48, 114.26) * mm});
            skLineSegment(sketch, "E297", {"start": v(658.48, 114.26) * mm, "end": v(652.83, 98.74) * mm});
            skLineSegment(sketch, "E298", {"start": v(652.83, 98.74) * mm, "end": v(644.45, 78.59) * mm});
            skLineSegment(sketch, "E299", {"start": v(644.45, 78.59) * mm, "end": v(635.07, 59.04) * mm});
            skLineSegment(sketch, "E300", {"start": v(635.07, 59.04) * mm, "end": v(624.67, 40.1) * mm});
            skLineSegment(sketch, "E301", {"start": v(624.67, 40.1) * mm, "end": v(613.26, 21.77) * mm});
            skLineSegment(sketch, "E302", {"start": v(613.26, 21.77) * mm, "end": v(600.83, 4.03) * mm});
            skLineSegment(sketch, "E303", {"start": v(600.83, 4.03) * mm, "end": v(587.4, -13.1) * mm});
            skLineSegment(sketch, "E304", {"start": v(587.4, -13.1) * mm, "end": v(576.66, -25.6) * mm});
            skLineSegment(sketch, "E305", {"start": v(576.66, -25.6) * mm, "end": v(572.95, -29.63) * mm});
            skLineSegment(sketch, "E306", {"start": v(572.95, -29.63) * mm, "end": v(569.2, -33.7) * mm});
            skLineSegment(sketch, "E307", {"start": v(569.2, -33.7) * mm, "end": v(557.43, -45.47) * mm});
            skLineSegment(sketch, "E308", {"start": v(557.43, -45.47) * mm, "end": v(540.8, -60.51) * mm});
            skLineSegment(sketch, "E309", {"start": v(540.8, -60.51) * mm, "end": v(523.06, -74.76) * mm});
            skLineSegment(sketch, "E310", {"start": v(523.06, -74.76) * mm, "end": v(504.21, -88.22) * mm});
            skLineSegment(sketch, "E311", {"start": v(504.21, -88.22) * mm, "end": v(484.26, -100.88) * mm});
            skLineSegment(sketch, "E312", {"start": v(484.26, -100.88) * mm, "end": v(463.2, -112.75) * mm});
            skLineSegment(sketch, "E313", {"start": v(463.2, -112.75) * mm, "end": v(441.02, -123.83) * mm});
            skLineSegment(sketch, "E314", {"start": v(441.02, -123.83) * mm, "end": v(423.62, -131.68) * mm});
            skLineSegment(sketch, "E315", {"start": v(423.62, -131.68) * mm, "end": v(417.74, -134.11) * mm});
            skLineSegment(sketch, "E316", {"start": v(417.74, -134.11) * mm, "end": v(411.7, -136.62) * mm});
            skLineSegment(sketch, "E317", {"start": v(411.7, -136.62) * mm, "end": v(393.26, -143.38) * mm});
            skLineSegment(sketch, "E318", {"start": v(393.26, -143.38) * mm, "end": v(367.52, -151.42) * mm});
            skLineSegment(sketch, "E319", {"start": v(367.52, -151.42) * mm, "end": v(340.51, -158.22) * mm});
            skLineSegment(sketch, "E320", {"start": v(340.51, -158.22) * mm, "end": v(312.23, -163.78) * mm});
            skLineSegment(sketch, "E321", {"start": v(312.23, -163.78) * mm, "end": v(282.69, -168.1) * mm});
            skLineSegment(sketch, "E322", {"start": v(282.69, -168.1) * mm, "end": v(251.88, -171.2) * mm});
            skLineSegment(sketch, "E323", {"start": v(251.88, -171.2) * mm, "end": v(219.8, -173.05) * mm});
            skLineSegment(sketch, "E324", {"start": v(219.8, -173.05) * mm, "end": v(194.8, -173.67) * mm});
            skLineSegment(sketch, "E325", {"start": v(194.8, -173.67) * mm, "end": v(186.46, -173.67) * mm});
            skLineSegment(sketch, "E326", {"start": v(186.46, -173.67) * mm, "end": v(-148.28, -173.67) * mm});
            skLineSegment(sketch, "E327", {"start": v(-148.28, -173.67) * mm, "end": v(-148.28, -693.04) * mm});
            skLineSegment(sketch, "E328", {"start": v(-148.28, -693.04) * mm, "end": v(-466.8, -693.04) * mm});
            skLineSegment(sketch, "E329", {"start": v(-466.8, -693.04) * mm, "end": v(-466.8, 755.51) * mm});
            skLineSegment(sketch, "E330", {"start": v(-466.8, 755.51) * mm, "end": v(186.46, 755.51) * mm});
            skCircle(sketch, "E331", {"center": v(-33.56, 31.54) * mm, "radius": 842.23 * mm});
            skSolve(sketch);
        }
        {
            var Q0;
            Q0=makeQuery(id+"F13.imprint","IMPRINT",FACE,{"disambiguationData":[TD([[makeQuery(id+"F13.imprint","IMPRINT",EDGE,{"derivedFrom":sQuery(id+"F13.wireOp",EDGE,"E171")}),-1.0]])]});
            extrude(context, id + "F14", {"entities" : qUnion([Q0]), "depth" : 177.8 * mm, "offsetDistance" : 25.4 * mm});
        }
        {
            var Q0;
            Q0=qCreatedBy(makeId("Top.planeOp"),FACE);
            var sketch = newSketch(context, id + "F15", { "sketchPlane" : qUnion([Q0])});
            skLineSegment(sketch, "E332.bottom", {"start": v(-1101.41, 355.55) * mm, "end": v(1068.36, 355.55) * mm});
            skLineSegment(sketch, "E332.top", {"start": v(-1101.41, 406.35) * mm, "end": v(1068.36, 406.35) * mm});
            skLineSegment(sketch, "E332.left", {"start": v(-1101.41, 355.55) * mm, "end": v(-1101.41, 406.35) * mm});
            skLineSegment(sketch, "E332.right", {"start": v(1068.36, 355.55) * mm, "end": v(1068.36, 406.35) * mm});
            skLineSegment(sketch, "E333.bottom", {"start": v(-1107.63, 0.2) * mm, "end": v(1069.56, 0.2) * mm});
            skLineSegment(sketch, "E333.top", {"start": v(-1107.63, -50.6) * mm, "end": v(1069.56, -50.6) * mm});
            skLineSegment(sketch, "E333.left", {"start": v(-1107.63, 0.2) * mm, "end": v(-1107.63, -50.6) * mm});
            skLineSegment(sketch, "E333.right", {"start": v(1069.56, 0.2) * mm, "end": v(1069.56, -50.6) * mm});
            skSolve(sketch);
        }
        {
            var Q0;
            Q0=makeQuery(id+"F15.imprint","IMPRINT",FACE,{"disambiguationData":[TD([[makeQuery(id+"F15.imprint","IMPRINT",EDGE,{"derivedFrom":sQuery(id+"F15.wireOp",EDGE,"E333.bottom")}),-1.0]])]});
            var Q1;
            Q1=makeQuery(id+"F15.imprint","IMPRINT",FACE,{"disambiguationData":[TD([[makeQuery(id+"F15.imprint","IMPRINT",EDGE,{"derivedFrom":sQuery(id+"F15.wireOp",EDGE,"E332.bottom")}),1.0]])]});
            extrude(context, id + "F16", {"entities" : qUnion([Q0, Q1]), "operationType" : NewBodyOperationType.REMOVE, "endBound" : BoundingType.THROUGH_ALL, "oppositeDirection" : true, "depth" : 25.4 * mm, "offsetDistance" : 25.4 * mm, "hasSecondDirection" : true, "secondDirectionBound" : SecondDirectionBoundingType.THROUGH_ALL, "secondDirectionOppositeDirection" : false, "secondDirectionDepth" : 25.4 * mm});
        }
        {
            var Q0;
            Q0=makeQuery(id+"F6.imprint","IMPRINT",FACE,{"disambiguationData":[TD([[makeQuery(id+"F6.imprint","IMPRINT",EDGE,{"derivedFrom":sQuery(id+"F6.wireOp",EDGE,"E7")}),1.0]])]});
            var sketch = newSketch(context, id + "F17", { "sketchPlane" : qUnion([Q0])});
            skCircle(sketch, "E334", {"center": v(-255.8, 641.9) * mm, "radius": 19.05 * mm});
            skCircle(sketch, "E335", {"center": v(-255.8, -53.15) * mm, "radius": 19.05 * mm});
            skCircle(sketch, "E336", {"center": v(-255.8, -593.07) * mm, "radius": 19.05 * mm});
            skCircle(sketch, "E337", {"center": v(298.23, 641.9) * mm, "radius": 19.05 * mm});
            skCircle(sketch, "E338", {"center": v(298.23, -53.15) * mm, "radius": 19.05 * mm});
            skCircle(sketch, "E339", {"center": v(594.38, 295.38) * mm, "radius": 19.05 * mm});
            skSolve(sketch);
        }
        {
            var Q0;
            Q0 = qSketchRegion(id + "F17", true);
            extrude(context, id + "F18", {"entities" : qUnion([Q0]), "depth" : 50.8 * mm, "offsetDistance" : 25.4 * mm});
        }
        {
            var Q0;
            Q0=makeQuery(id+"F16.boolean.opBoolean","COPY",FACE,{"disambiguationData":[TD([makeQuery(id+"F10.opExtrude","SWEPT_FACE",FACE,{"disambiguationData":[OSD([sQuery(id+"F6.wireOp",EDGE,"E7")])]})])],"derivedFrom":makeQuery(id+"F16.opExtrude","SWEPT_FACE",FACE,{"disambiguationData":[OSD([sQuery(id+"F15.wireOp",EDGE,"E333.bottom")])]})});
            var sketch = newSketch(context, id + "F19", { "sketchPlane" : qUnion([Q0])});
            skCircle(sketch, "E340", {"center": v(-312.27, 641.98) * mm, "radius": 19.05 * mm});
            skCircle(sketch, "E341", {"center": v(-312.27, -53.07) * mm, "radius": 19.05 * mm});
            skCircle(sketch, "E342", {"center": v(-312.27, -593) * mm, "radius": 19.05 * mm});
            skCircle(sketch, "E343", {"center": v(241.76, 641.98) * mm, "radius": 19.05 * mm});
            skCircle(sketch, "E344", {"center": v(241.76, -53.07) * mm, "radius": 19.05 * mm});
            skCircle(sketch, "E345", {"center": v(537.91, 295.46) * mm, "radius": 19.05 * mm});
            skSolve(sketch);
        }
        {
            var Q0;
            Q0 = qSketchRegion(id + "F19", true);
            extrude(context, id + "F20", {"entities" : qUnion([Q0]), "depth" : 50.8 * mm, "offsetDistance" : 25.4 * mm});
        }
    });
